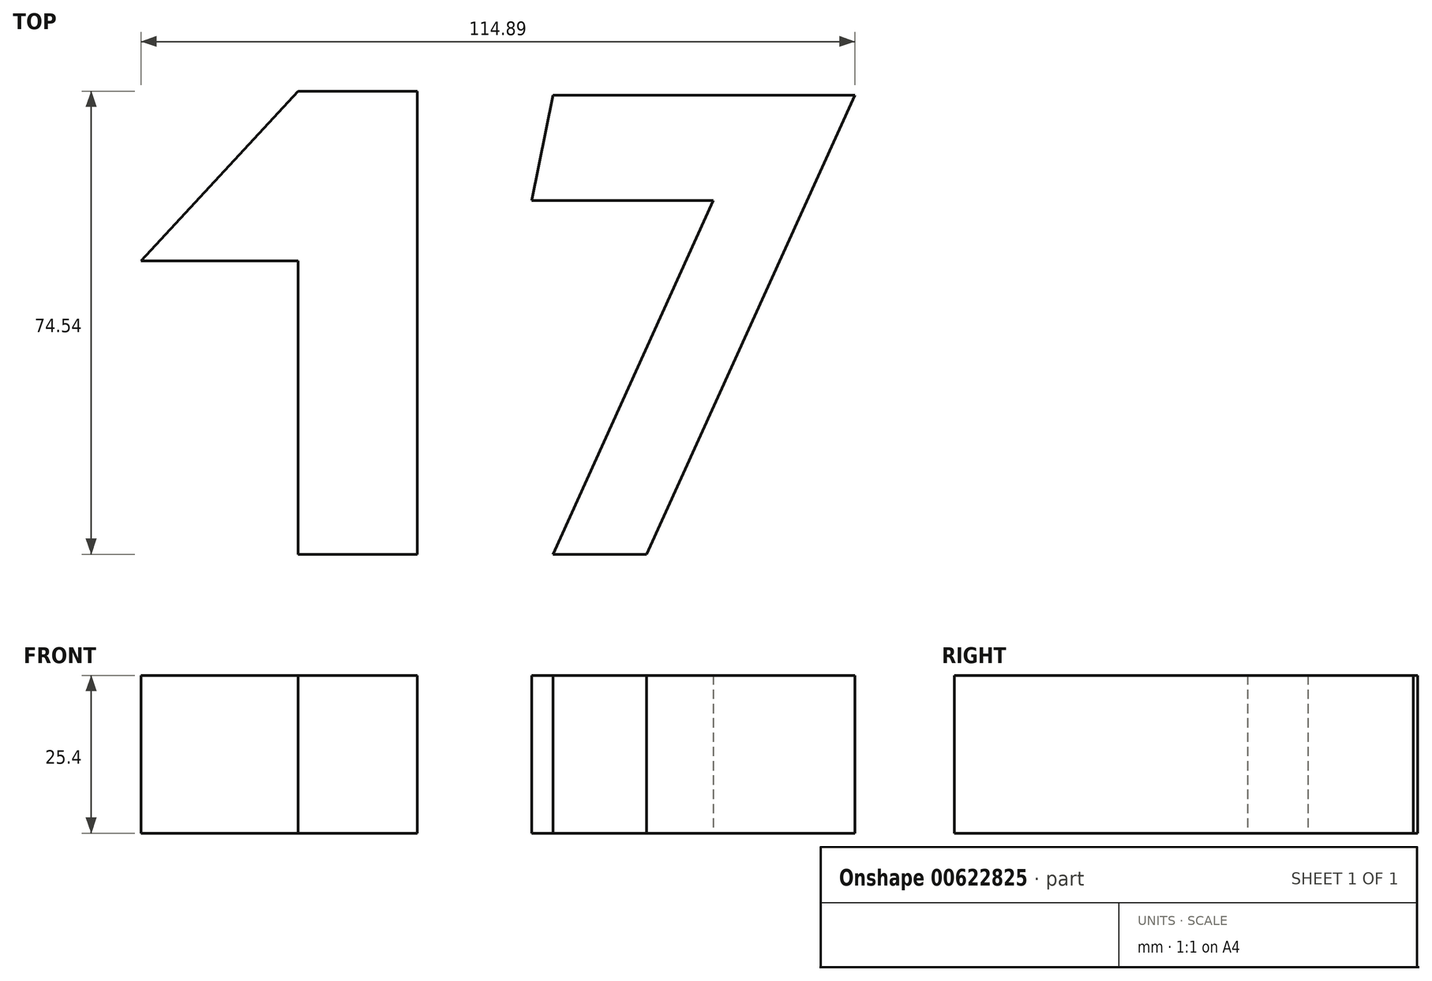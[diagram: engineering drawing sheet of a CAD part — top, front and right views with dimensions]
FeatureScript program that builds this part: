
annotation { "Feature Type Name" : "Feature", "Feature Type Description" : "" }
export const myFeature = defineFeature(function(context is Context, id is Id, definition is map)
    precondition{}
    {
        {
            var Q0;
            Q0=qCreatedBy(makeId("Top.planeOp"),FACE);
            var sketch = newSketch(context, id + "F0", { "sketchPlane" : qUnion([Q0])});
            skLineSegment(sketch, "E0", {"start": v(-29.92, 56.93) * mm, "end": v(-10.77, 56.93) * mm});
            skLineSegment(sketch, "E1", {"start": v(-10.77, 56.93) * mm, "end": v(-10.77, -17.6) * mm});
            skLineSegment(sketch, "E2", {"start": v(-10.77, -17.6) * mm, "end": v(-29.92, -17.6) * mm});
            skLineSegment(sketch, "E3", {"start": v(-29.92, 56.93) * mm, "end": v(-55.22, 29.58) * mm});
            skLineSegment(sketch, "E4", {"start": v(-55.22, 29.58) * mm, "end": v(-29.92, 29.58) * mm});
            skLineSegment(sketch, "E5", {"start": v(-29.92, 29.58) * mm, "end": v(-29.92, -17.6) * mm});
            skLineSegment(sketch, "E6", {"start": v(11.11, 56.25) * mm, "end": v(59.67, 56.25) * mm});
            skLineSegment(sketch, "E7", {"start": v(59.67, 56.25) * mm, "end": v(26.16, -17.6) * mm});
            skLineSegment(sketch, "E8", {"start": v(26.16, -17.6) * mm, "end": v(11.08, -17.6) * mm});
            skLineSegment(sketch, "E9", {"start": v(11.08, -17.6) * mm, "end": v(36.9, 39.3) * mm});
            skLineSegment(sketch, "E10", {"start": v(36.9, 39.3) * mm, "end": v(7.7, 39.3) * mm});
            skLineSegment(sketch, "E11", {"start": v(7.7, 39.3) * mm, "end": v(11.11, 56.25) * mm});
            skSolve(sketch);
        }
        {
            var Q0;
            Q0 = qSketchRegion(id + "F0", true);
            extrude(context, id + "F1", {"entities" : qUnion([Q0]), "depth" : 25.4 * mm, "offsetDistance" : 25.4 * mm});
        }
    });
